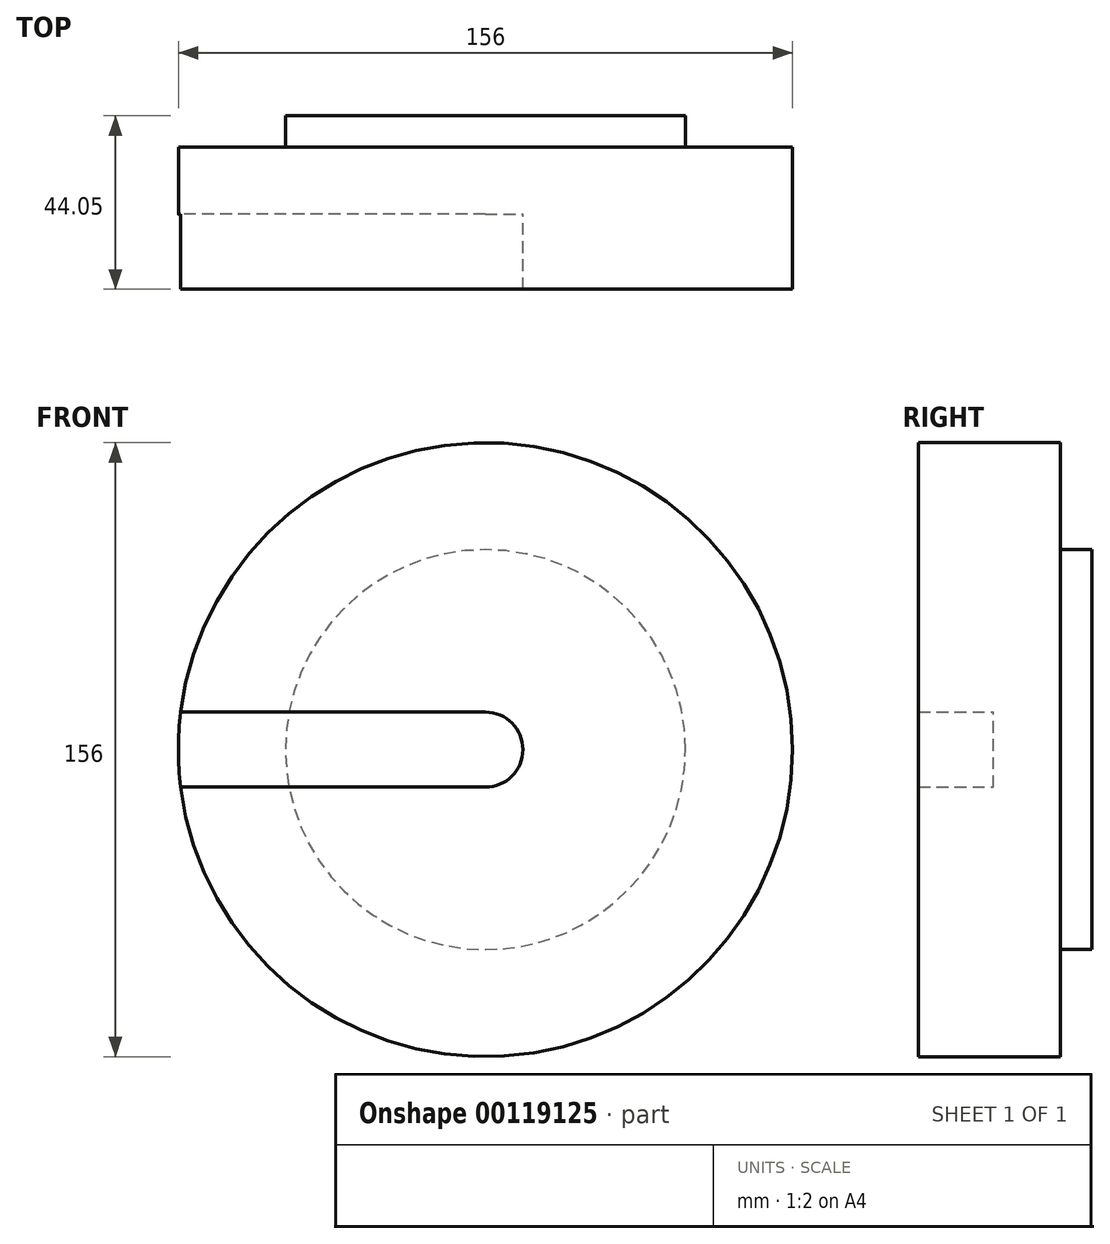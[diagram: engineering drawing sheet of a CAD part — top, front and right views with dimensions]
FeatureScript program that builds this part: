
annotation { "Feature Type Name" : "Feature", "Feature Type Description" : "" }
export const myFeature = defineFeature(function(context is Context, id is Id, definition is map)
    precondition{}
    {
        {
            var Q0;
            Q0=qCreatedBy(makeId("Front.planeOp"),FACE);
            var sketch = newSketch(context, id + "F0", { "sketchPlane" : qUnion([Q0])});
            skCircle(sketch, "E0", {"center": v(0, 0) * mm, "radius": 50.8 * mm});
            skSolve(sketch);
        }
        {
            var Q0;
            Q0=makeQuery(id+"F0.imprint","IMPRINT",FACE,{"disambiguationData":[TD([[makeQuery(id+"F0.imprint","IMPRINT",EDGE,{"derivedFrom":sQuery(id+"F0.wireOp",EDGE,"E0")}),1.0]])]});
            extrude(context, id + "F1", {"entities" : qUnion([Q0]), "depth" : 8 * mm});
        }
        {
            var Q0;
            Q0=makeQuery(id+"F1.opExtrude","CAP_FACE",FACE,{"disambiguationData":[OSD([sQuery(id+"F0.wireOp",EDGE,"E0")])],"isStart":false});
            var sketch = newSketch(context, id + "F2", { "sketchPlane" : qUnion([Q0])});
            skCircle(sketch, "E1", {"center": v(0, 0) * mm, "radius": 78 * mm});
            skSolve(sketch);
        }
        {
            var Q0;
            Q0=makeQuery(id+"F2.imprint","IMPRINT",FACE,{"disambiguationData":[TD([[makeQuery(id+"F2.imprint","IMPRINT",EDGE,{"derivedFrom":sQuery(id+"F2.wireOp",EDGE,"E1")}),1.0]])]});
            var Q1;
            Q1=makeQuery(id+"F2.imprint","IMPRINT",FACE,{"disambiguationData":[TD([[makeQuery(id+"F2.imprint","IMPRINT",EDGE,{"derivedFrom":makeQuery(id+"F1.opExtrude","CAP_EDGE",EDGE,{"disambiguationData":[OSD([sQuery(id+"F0.wireOp",EDGE,"E0")])],"isStart":false})}),1.0]])]});
            extrude(context, id + "F3", {"entities" : qUnion([Q0, Q1]), "operationType" : NewBodyOperationType.ADD, "depth" : (72 - 55) * mm});
        }
        {
            var Q0;
            Q0=makeQuery(id+"F3.opExtrude","CAP_FACE",FACE,{"disambiguationData":[OSD([sQuery(id+"F2.wireOp",EDGE,"E1")])],"isStart":false});
            var sketch = newSketch(context, id + "F4", { "sketchPlane" : qUnion([Q0])});
            skLineSegment(sketch, "E2", {"start": v(0, 0) * mm, "end": v(-182.47, 0) * mm});
            skArc(sketch, "E3.0.startCap", {"start": v(0, 9.53) * mm, "mid": v(9.53, 0) * mm, "end": v(0, -9.53) * mm});
            skArc(sketch, "E3.0.endCap", {"start": v(-182.47, -9.53) * mm, "mid": v(-192, 0) * mm, "end": v(-182.47, 9.52) * mm});
            skLineSegment(sketch, "E3.0.left", {"start": v(0, -9.53) * mm, "end": v(-182.47, -9.53) * mm});
            skLineSegment(sketch, "E3.0.right", {"start": v(0, 9.53) * mm, "end": v(-182.47, 9.53) * mm});
            skSolve(sketch);
        }
        {
            var Q0;
            {var subQ5=sQuery(id+"F4.wireOp",EDGE,"E3.0.endCap");Q0=makeQuery(id+"F4.imprint","IMPRINT",FACE,{"disambiguationData":[TD([[makeQuery(id+"F4.imprint","IMPRINT",EDGE,{"derivedFrom":subQ5}),-1.0]])]});}
            var Q1;
            {var subQ5=sQuery(id+"F4.wireOp",EDGE,"E3.0.startCap");Q1=makeQuery(id+"F4.imprint","IMPRINT",FACE,{"disambiguationData":[TD([[makeQuery(id+"F4.imprint","IMPRINT",EDGE,{"derivedFrom":subQ5}),-1.0]])]});}
            extrude(context, id + "F5", {"entities" : qUnion([Q0, Q1]), "operationType" : NewBodyOperationType.ADD, "depth" : 19.05 * mm});
        }
    });
